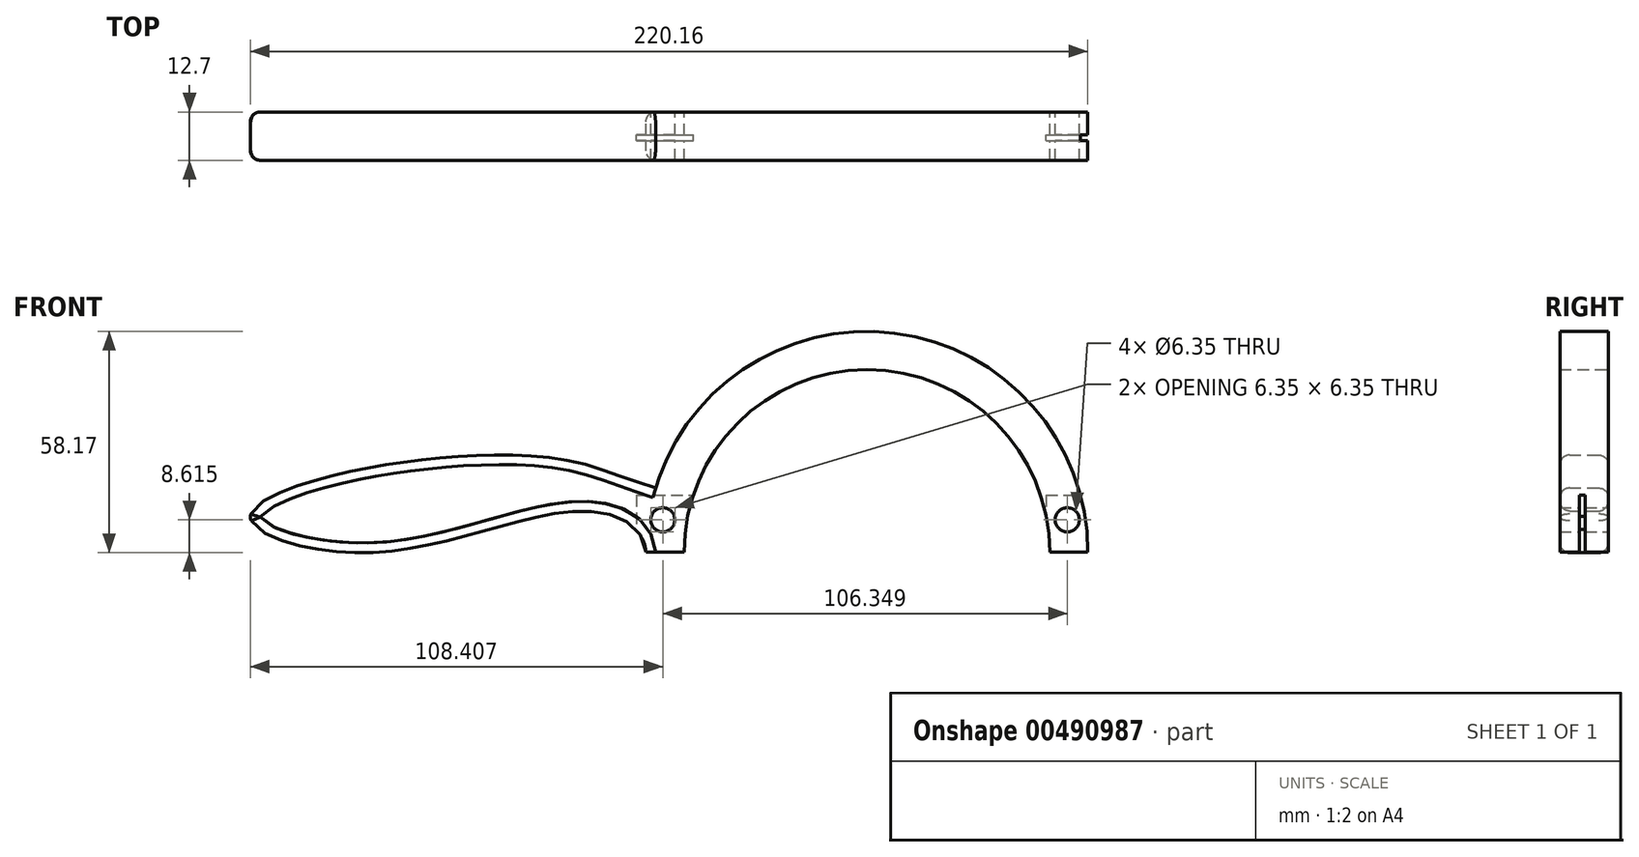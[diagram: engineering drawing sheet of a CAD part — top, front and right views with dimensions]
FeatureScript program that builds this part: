
annotation { "Feature Type Name" : "Feature", "Feature Type Description" : "" }
export const myFeature = defineFeature(function(context is Context, id is Id, definition is map)
    precondition{}
    {
        {
            var Q0;
            Q0=qCreatedBy(makeId("Front.planeOp"),FACE);
            var sketch = newSketch(context, id + "F0", { "sketchPlane" : qUnion([Q0])});
            skArc(sketch, "E0", {"start": v(58.08, 0) * mm, "mid": v(8.53, 57.45) * mm, "end": v(-55.57, 16.88) * mm});
            skArc(sketch, "E1", {"start": v(48.05, 0) * mm, "mid": v(0, 48.05) * mm, "end": v(-48.05, 0) * mm});
            skLineSegment(sketch, "E2", {"start": v(-58.08, 0) * mm, "end": v(-48.05, 0) * mm});
            skLineSegment(sketch, "E3.trimOffspring", {"start": v(48.05, 0) * mm, "end": v(58.08, 0) * mm});
            skFitSpline(sketch, "E4", {"points": [v(-58.08, 0) * mm, v(-73.9, 10.84) * mm, v(-129.1, 0) * mm, v(-162.04, 8.81) * mm, v(-139.5, 20.37) * mm, v(-81.7, 24.7) * mm, v(-55.57, 16.88) * mm], "startDerivative": vector(-10.6, 164.34) * mm, "endDerivative": vector(210.03, -63.36) * mm});
            skCircle(sketch, "E5", {"center": v(-53.67, 8.53) * mm, "radius": 3.18 * mm});
            skCircle(sketch, "E6", {"center": v(52.68, 8.53) * mm, "radius": 3.18 * mm});
            skPoint(sketch, "E7", {"position": v(33.63, 47.36) * mm});
            skSolve(sketch);
        }
        {
            var Q0;
            Q0 = qSketchRegion(id + "F0", true);
            extrude(context, id + "F1", {"entities" : qUnion([Q0]), "depth" : 12.7 * mm});
        }
        {
            var Q0;
            Q0=makeQuery(id+"F1.opExtrude","CAP_EDGE",EDGE,{"disambiguationData":[OSD([sQuery(id+"F0.wireOp",EDGE,"E4")])],"isStart":false});
            fillet(context, id + "F2", {"entities" : qUnion([Q0]), "radius" : 2.54 * mm, "tangentPropagation" : true, "allowEdgeOverflow" : false});
        }
        {
            var Q0;
            Q0=makeQuery(id+"F1.opExtrude","CAP_EDGE",EDGE,{"disambiguationData":[OSD([sQuery(id+"F0.wireOp",EDGE,"E4")])],"isStart":true});
            fillet(context, id + "F3", {"entities" : qUnion([Q0]), "radius" : 2.54 * mm, "tangentPropagation" : true, "allowEdgeOverflow" : false});
        }
        {
            var Q0;
            Q0=qCreatedBy(makeId("Top.planeOp"),FACE);
            var sketch = newSketch(context, id + "F4", { "sketchPlane" : qUnion([Q0])});
            skLineSegment(sketch, "E8.bottom", {"start": v(-60.64, -7.56) * mm, "end": v(-44.5, -7.56) * mm});
            skLineSegment(sketch, "E8.top", {"start": v(-60.64, -6.06) * mm, "end": v(-44.5, -6.06) * mm});
            skLineSegment(sketch, "E8.left", {"start": v(-60.64, -7.56) * mm, "end": v(-60.64, -6.06) * mm});
            skLineSegment(sketch, "E8.right", {"start": v(-44.5, -7.56) * mm, "end": v(-44.5, -6.06) * mm});
            skLineSegment(sketch, "E9.bottom", {"start": v(47.11, -6.06) * mm, "end": v(59.11, -6.06) * mm});
            skLineSegment(sketch, "E9.top", {"start": v(47.11, -7.56) * mm, "end": v(59.11, -7.56) * mm});
            skLineSegment(sketch, "E9.left", {"start": v(47.11, -6.06) * mm, "end": v(47.11, -7.56) * mm});
            skLineSegment(sketch, "E9.right", {"start": v(59.11, -6.06) * mm, "end": v(59.11, -7.56) * mm});
            skSolve(sketch);
        }
        {
            var Q0;
            Q0 = qSketchRegion(id + "F4", true);
            extrude(context, id + "F5", {"entities" : qUnion([Q0]), "operationType" : NewBodyOperationType.REMOVE, "depth" : 15 * mm});
        }
    });
